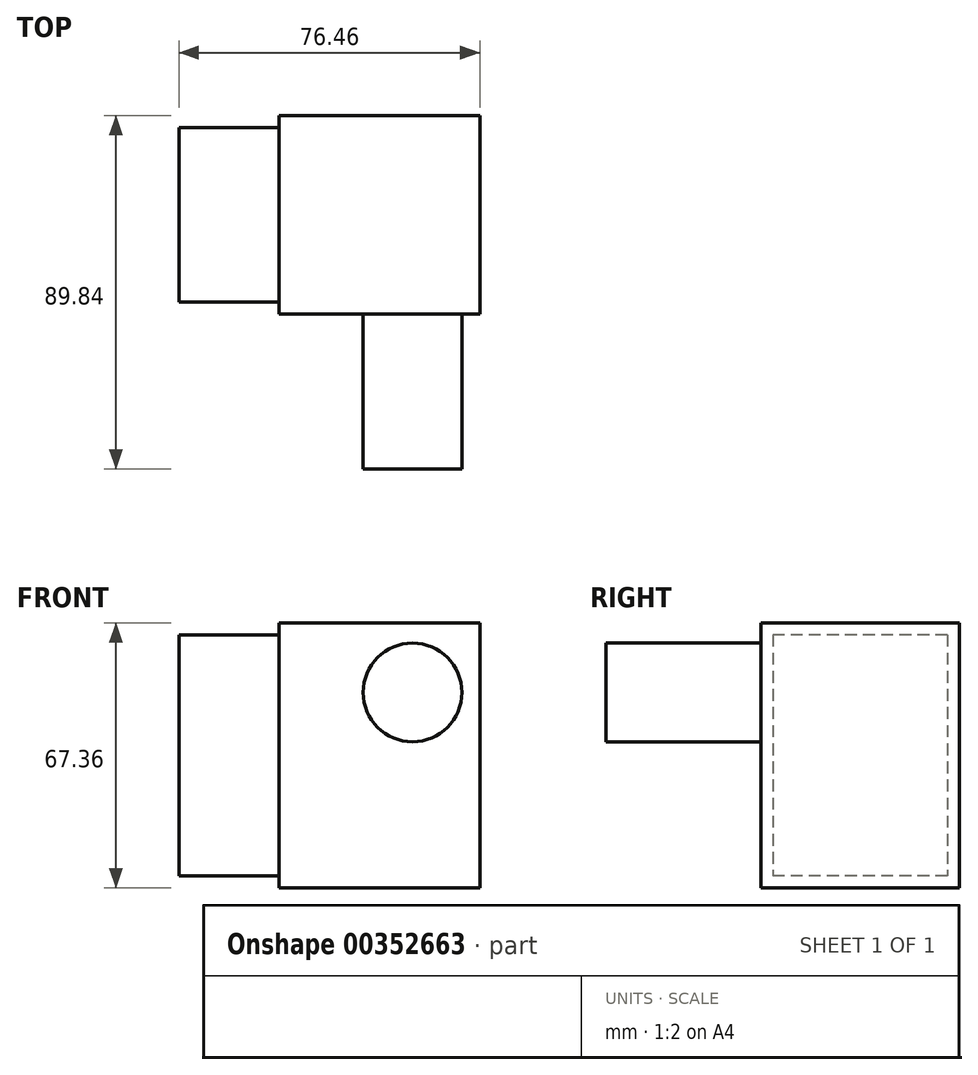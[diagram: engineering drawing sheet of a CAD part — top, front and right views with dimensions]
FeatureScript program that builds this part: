
annotation { "Feature Type Name" : "Feature", "Feature Type Description" : "" }
export const myFeature = defineFeature(function(context is Context, id is Id, definition is map)
    precondition{}
    {
        {
            var Q0;
            Q0=qCreatedBy(makeId("Top.planeOp"),FACE);
            var sketch = newSketch(context, id + "F0", { "sketchPlane" : qUnion([Q0])});
            skLineSegment(sketch, "E0.bottom", {"start": v(24.73, 35.75) * mm, "end": v(-26.33, 35.75) * mm});
            skLineSegment(sketch, "E0.top", {"start": v(24.73, -14.7) * mm, "end": v(-26.33, -14.7) * mm});
            skLineSegment(sketch, "E0.left", {"start": v(24.73, 35.75) * mm, "end": v(24.73, -14.7) * mm});
            skLineSegment(sketch, "E0.right", {"start": v(-26.33, 35.75) * mm, "end": v(-26.33, -14.7) * mm});
            skSolve(sketch);
        }
        {
            var Q0;
            Q0 = qSketchRegion(id + "F0", true);
            extrude(context, id + "F1", {"entities" : qUnion([Q0]), "depth" : 67.36 * mm});
        }
        {
            var Q0;
            Q0=makeQuery(id+"F1.opExtrude","SWEPT_FACE",FACE,{"disambiguationData":[OSD([sQuery(id+"F0.wireOp",EDGE,"E0.top")])]});
            var sketch = newSketch(context, id + "F2", { "sketchPlane" : qUnion([Q0])});
            skCircle(sketch, "E1", {"center": v(7.65, 49.64) * mm, "radius": 12.56 * mm});
            skSolve(sketch);
        }
        {
            var Q0;
            Q0 = qSketchRegion(id + "F2", true);
            extrude(context, id + "F3", {"entities" : qUnion([Q0]), "operationType" : NewBodyOperationType.ADD, "depth" : 39.38 * mm});
        }
        {
            var Q0;
            Q0=makeQuery(id+"F1.opExtrude","SWEPT_FACE",FACE,{"disambiguationData":[OSD([sQuery(id+"F0.wireOp",EDGE,"E0.right")])]});
            var sketch = newSketch(context, id + "F4", { "sketchPlane" : qUnion([Q0])});
            skLineSegment(sketch, "E2.0", {"start": v(-35.75, 64.31) * mm, "end": v(14.7, 64.31) * mm});
            skLineSegment(sketch, "E3.0", {"start": v(-32.7, 67.36) * mm, "end": v(-32.7, 0) * mm});
            skLineSegment(sketch, "E4.0", {"start": v(11.66, 67.36) * mm, "end": v(11.66, 0) * mm});
            skLineSegment(sketch, "E5.0", {"start": v(-35.75, 3.05) * mm, "end": v(14.7, 3.05) * mm});
            skSolve(sketch);
        }
        {
            var Q0;
            {var subQ0=sQuery(id+"F4.wireOp",EDGE,"E3.0");var subQ1=sQuery(id+"F4.wireOp",EDGE,"E2.0");var subQ2=makeQuery(id+"F4.imprint","INTERSECT",VERTEX,{"derivedFrom":[subQ1,subQ0]});Q0=makeQuery(id+"F4.imprint","IMPRINT",FACE,{"disambiguationData":[TD([[makeQuery(id+"F4.imprint","IMPRINT",EDGE,{"disambiguationData":[TD([[subQ2,-1.0]])],"derivedFrom":subQ1}),-1.0]])]});}
            extrude(context, id + "F5", {"entities" : qUnion([Q0]), "operationType" : NewBodyOperationType.ADD, "depth" : 25.4 * mm});
        }
    });
